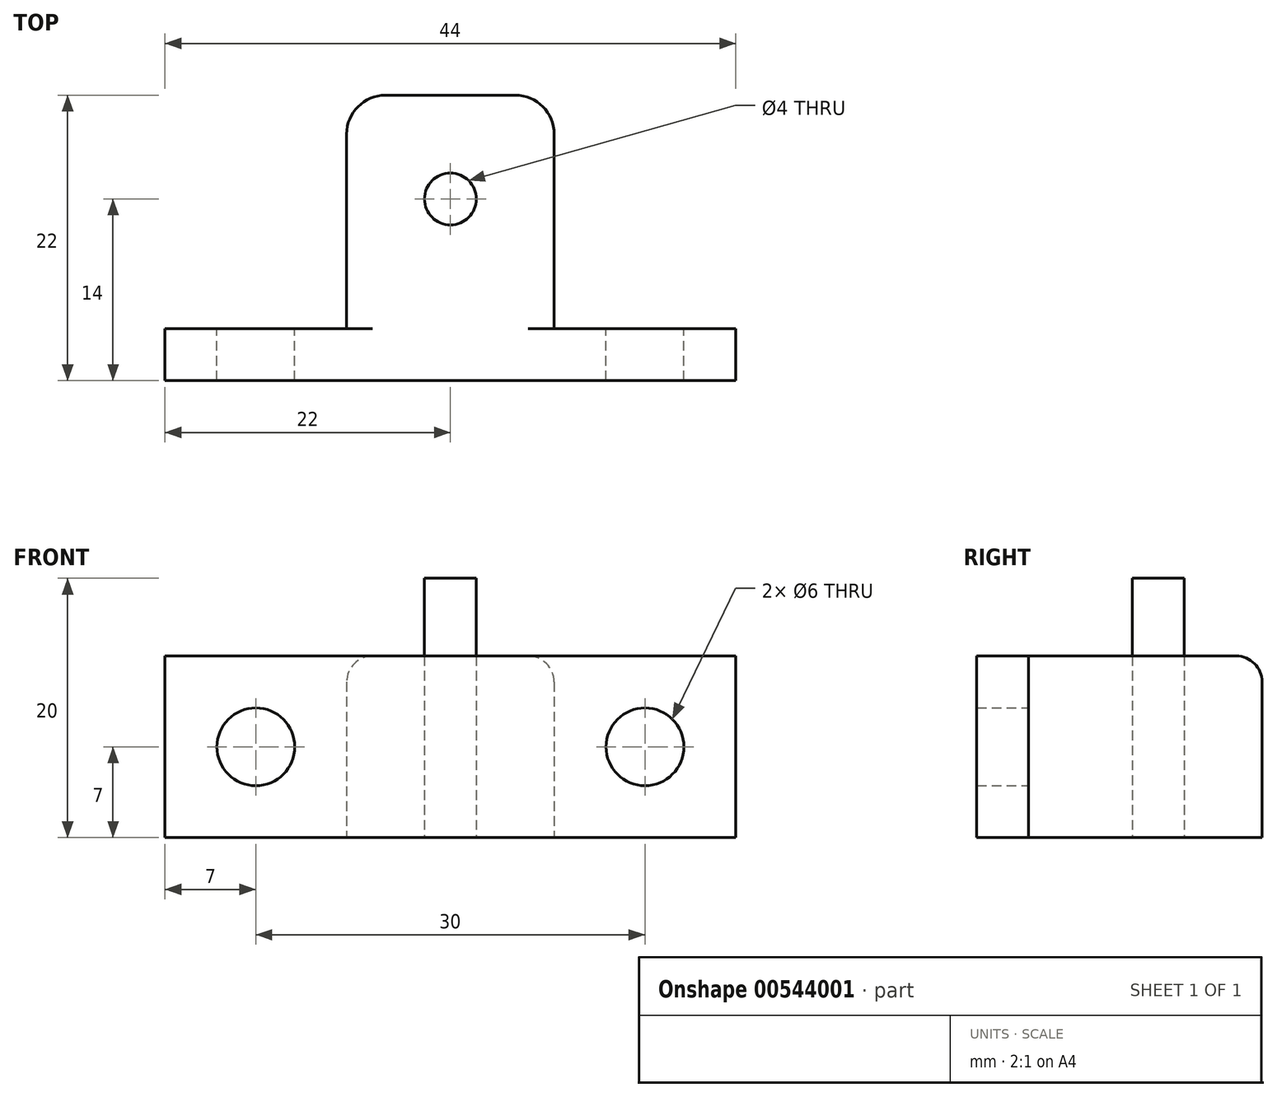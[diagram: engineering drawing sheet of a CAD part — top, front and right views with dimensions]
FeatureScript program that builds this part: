
annotation { "Feature Type Name" : "Feature", "Feature Type Description" : "" }
export const myFeature = defineFeature(function(context is Context, id is Id, definition is map)
    precondition{}
    {
        {
            var Q0;
            Q0=qCreatedBy(makeId("Top.planeOp"),FACE);
            var sketch = newSketch(context, id + "F0", { "sketchPlane" : qUnion([Q0])});
            skLineSegment(sketch, "E0", {"start": v(-60.28, 0) * mm, "end": v(64.69, 0) * mm, "construction": true});
            skLineSegment(sketch, "E1", {"start": v(0, 50.56) * mm, "end": v(0, -93.6) * mm, "construction": true});
            skLineSegment(sketch, "E2", {"start": v(-8, 8) * mm, "end": v(8, 8) * mm});
            skLineSegment(sketch, "E3", {"start": v(8, 8) * mm, "end": v(8, -10) * mm});
            skLineSegment(sketch, "E4", {"start": v(8, -10) * mm, "end": v(22, -10) * mm});
            skLineSegment(sketch, "E5", {"start": v(22, -10) * mm, "end": v(22, -14) * mm});
            skLineSegment(sketch, "E6", {"start": v(22, -14) * mm, "end": v(-22, -14) * mm});
            skLineSegment(sketch, "E7", {"start": v(-22, -14) * mm, "end": v(-22, -10) * mm});
            skLineSegment(sketch, "E8", {"start": v(-22, -10) * mm, "end": v(-8, -10) * mm});
            skLineSegment(sketch, "E9", {"start": v(-8, -10) * mm, "end": v(-8, 8) * mm});
            skCircle(sketch, "E10", {"center": v(0, 0) * mm, "radius": 2 * mm});
            skSolve(sketch);
        }
        {
            var Q0;
            Q0=makeQuery(id+"F0.imprint","IMPRINT",FACE,{"disambiguationData":[TD([[makeQuery(id+"F0.imprint","IMPRINT",EDGE,{"derivedFrom":sQuery(id+"F0.wireOp",EDGE,"E10")}),1.0]])]});
            extrude(context, id + "F1", {"entities" : qUnion([Q0]), "depth" : 20 * mm, "offsetDistance" : 25 * mm});
        }
        {
            var Q0;
            Q0 = qSketchRegion(id + "F0", true);
            extrude(context, id + "F2", {"entities" : qUnion([Q0]), "depth" : 14 * mm, "offsetDistance" : 25 * mm});
        }
        {
            var Q0;
            Q0=makeQuery(id+"F2.opExtrude","SWEPT_FACE",FACE,{"disambiguationData":[OSD([sQuery(id+"F0.wireOp",EDGE,"E8")])]});
            var sketch = newSketch(context, id + "F3", { "sketchPlane" : qUnion([Q0])});
            skLineSegment(sketch, "E11", {"start": v(15, 14) * mm, "end": v(15, 0) * mm, "construction": true});
            skLineSegment(sketch, "E12", {"start": v(22, 7) * mm, "end": v(8, 7) * mm, "construction": true});
            skCircle(sketch, "E13", {"center": v(15, 7) * mm, "radius": 3 * mm});
            skSolve(sketch);
        }
        {
            var Q0;
            Q0=makeQuery(id+"F2.opExtrude","SWEPT_FACE",FACE,{"disambiguationData":[OSD([sQuery(id+"F0.wireOp",EDGE,"E4")])]});
            var sketch = newSketch(context, id + "F4", { "sketchPlane" : qUnion([Q0])});
            skLineSegment(sketch, "E14", {"start": v(-15, 14) * mm, "end": v(-15, 0) * mm, "construction": true});
            skPoint(sketch, "E14.endSnap0", {"position": v(-15, 0) * mm});
            skLineSegment(sketch, "E15", {"start": v(-22, 7) * mm, "end": v(-8, 7) * mm, "construction": true});
            skPoint(sketch, "E16.orphan", {"position": v(-15, -0.5) * mm});
            skCircle(sketch, "E17", {"center": v(-15, 7) * mm, "radius": 3 * mm});
            skSolve(sketch);
        }
        {
            var Q0;
            Q0=makeQuery(id+"F3.imprint","IMPRINT",FACE,{"disambiguationData":[TD([[makeQuery(id+"F3.imprint","IMPRINT",EDGE,{"derivedFrom":sQuery(id+"F3.wireOp",EDGE,"E13")}),1.0]])]});
            extrude(context, id + "F5", {"entities" : qUnion([Q0]), "operationType" : NewBodyOperationType.REMOVE, "endBound" : BoundingType.THROUGH_ALL, "oppositeDirection" : true, "depth" : 25 * mm, "offsetDistance" : 25 * mm});
        }
        {
            var Q0;
            Q0=makeQuery(id+"F4.imprint","IMPRINT",FACE,{"disambiguationData":[TD([[makeQuery(id+"F4.imprint","IMPRINT",EDGE,{"derivedFrom":sQuery(id+"F4.wireOp",EDGE,"E17")}),1.0]])]});
            extrude(context, id + "F6", {"entities" : qUnion([Q0]), "operationType" : NewBodyOperationType.REMOVE, "endBound" : BoundingType.THROUGH_ALL, "oppositeDirection" : true, "depth" : 25 * mm, "offsetDistance" : 25 * mm});
        }
        {
            var Q0;
            Q0=makeQuery(id+"F2.opExtrude","SWEPT_EDGE",EDGE,{"disambiguationData":[OSD([sQuery(id+"F0.wireOp",EDGE,"E2"),sQuery(id+"F0.wireOp",EDGE,"E9")])]});
            fillet(context, id + "F7", {"entities" : qUnion([Q0]), "radius" : 3 * mm, "tangentPropagation" : true, "allowEdgeOverflow" : false});
        }
        {
            var Q0;
            Q0=makeQuery(id+"F2.opExtrude","SWEPT_EDGE",EDGE,{"disambiguationData":[OSD([sQuery(id+"F0.wireOp",EDGE,"E2"),sQuery(id+"F0.wireOp",EDGE,"E3")])]});
            fillet(context, id + "F8", {"entities" : qUnion([Q0]), "radius" : 3 * mm, "tangentPropagation" : true, "allowEdgeOverflow" : false});
        }
        {
            var Q0;
            Q0=makeQuery(id+"F2.opExtrude","CAP_EDGE",EDGE,{"disambiguationData":[OSD([sQuery(id+"F0.wireOp",EDGE,"E9")])],"isStart":false});
            fillet(context, id + "F9", {"entities" : qUnion([Q0]), "radius" : 2 * mm, "tangentPropagation" : true, "allowEdgeOverflow" : false});
        }
    });
